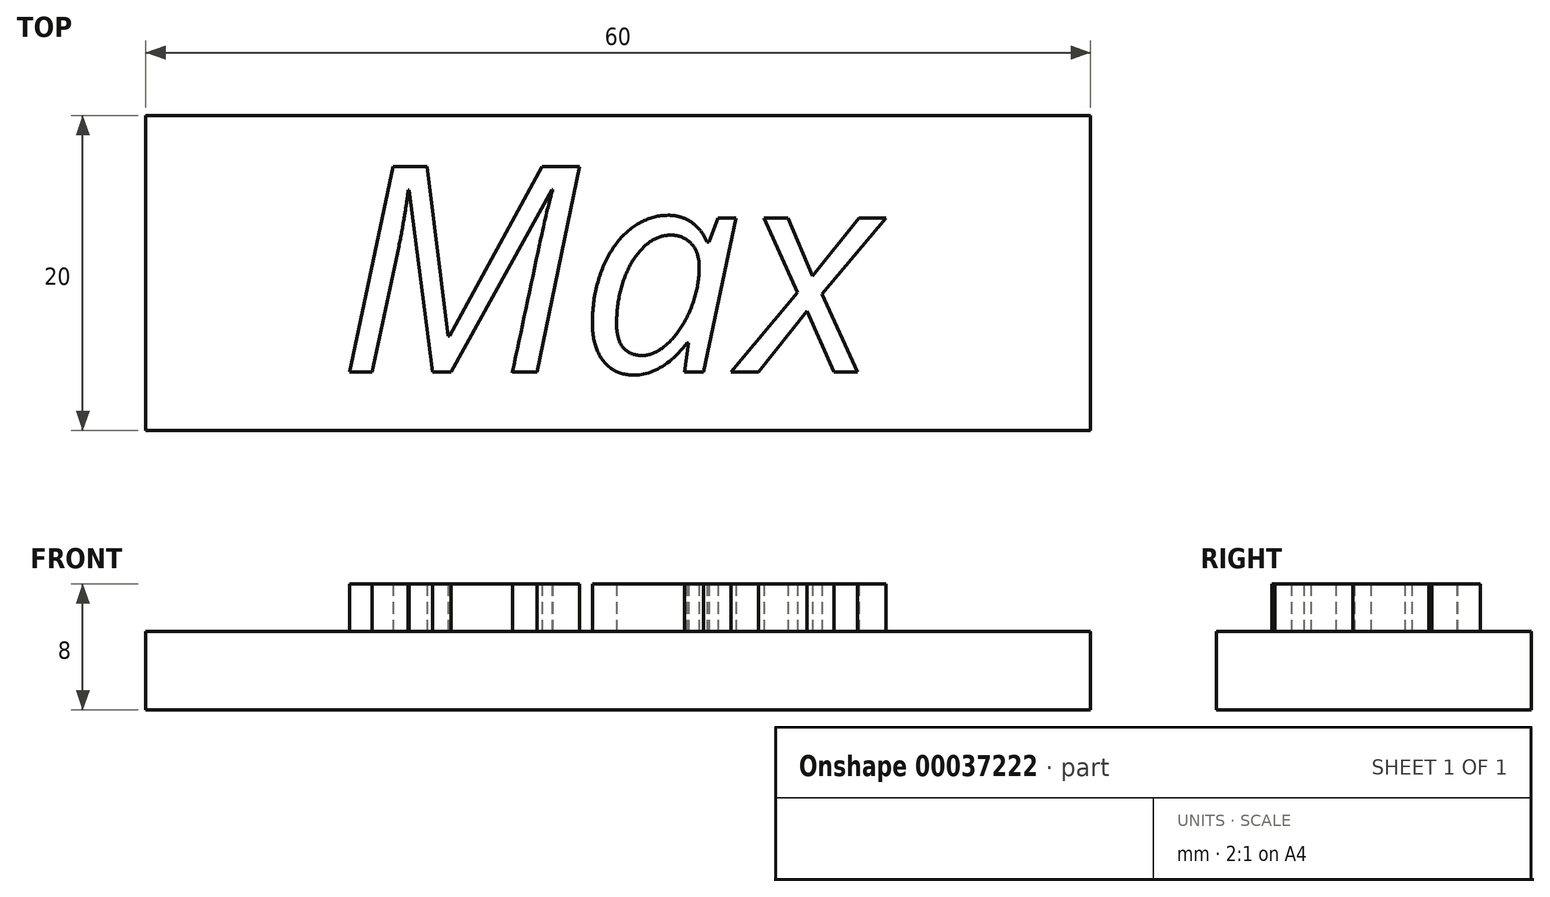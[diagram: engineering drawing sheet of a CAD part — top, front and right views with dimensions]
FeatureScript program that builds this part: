
annotation { "Feature Type Name" : "Feature", "Feature Type Description" : "" }
export const myFeature = defineFeature(function(context is Context, id is Id, definition is map)
    precondition{}
    {
        {
            var Q0;
            Q0=qCreatedBy(makeId("Top.planeOp"),FACE);
            var sketch = newSketch(context, id + "F0", { "sketchPlane" : qUnion([Q0])});
            skLineSegment(sketch, "E0.rect.bottom", {"start": v(30, 10) * mm, "end": v(-30, 10) * mm});
            skLineSegment(sketch, "E0.rect.top", {"start": v(30, -10) * mm, "end": v(-30, -10) * mm});
            skLineSegment(sketch, "E0.rect.left", {"start": v(30, 10) * mm, "end": v(30, -10) * mm});
            skLineSegment(sketch, "E0.rect.right", {"start": v(-30, 10) * mm, "end": v(-30, -10) * mm});
            skPoint(sketch, "E0.rect.middle", {"position": v(0, 0) * mm});
            skSolve(sketch);
        }
        {
            var Q0;
            Q0 = qSketchRegion(id + "F0", true);
            extrude(context, id + "F1", {"entities" : qUnion([Q0]), "depth" : 5 * mm});
        }
        {
            var Q0;
            Q0=makeQuery(id+"F1.opExtrude","CAP_FACE",FACE,{"disambiguationData":[OSD([sQuery(id+"F0.wireOp",EDGE,"E0.rect.bottom"),sQuery(id+"F0.wireOp",EDGE,"E0.rect.top"),sQuery(id+"F0.wireOp",EDGE,"E0.rect.left"),sQuery(id+"F0.wireOp",EDGE,"E0.rect.right")])],"isStart":false});
            var sketch = newSketch(context, id + "F2", { "sketchPlane" : qUnion([Q0])});
            skText(sketch, "E1", { "text": "Max", "fontName": "OpenSans-Italic.ttf"});
            const initialGuessF2  = {"E1": [-0.01782, -0.0063, 1, 0, 0.01317]};
            skSetInitialGuess(sketch, initialGuessF2);
            skSolve(sketch);
        }
        {
            var Q0;
            Q0 = qSketchRegion(id + "F2", true);
            extrude(context, id + "F3", {"entities" : qUnion([Q0]), "operationType" : NewBodyOperationType.ADD, "depth" : 3 * mm});
        }
    });
